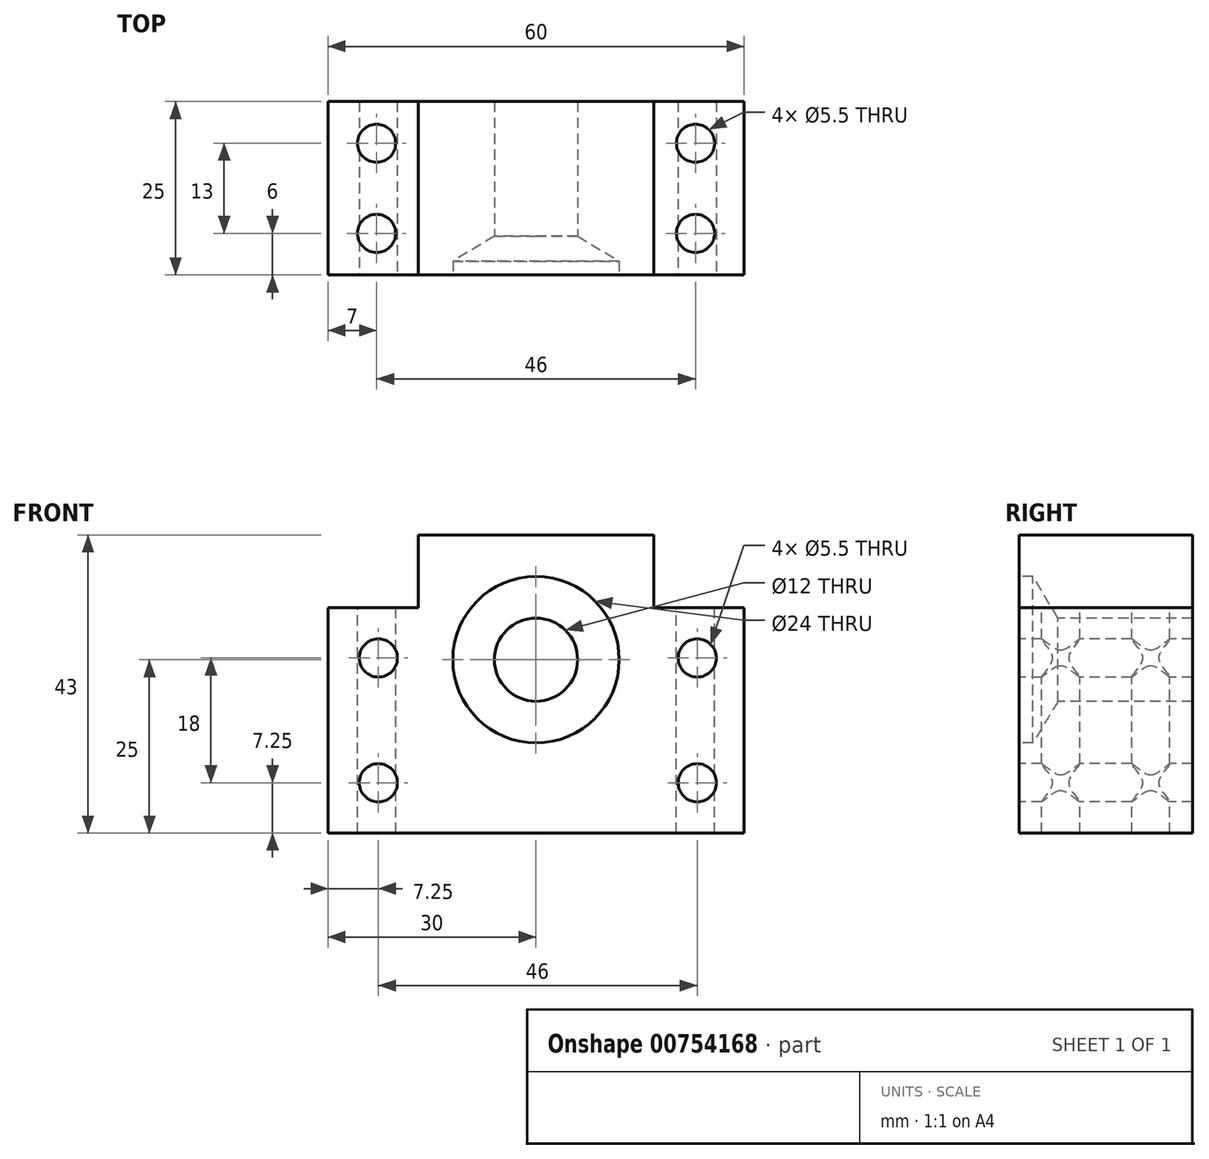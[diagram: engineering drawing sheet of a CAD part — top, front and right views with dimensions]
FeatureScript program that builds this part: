
annotation { "Feature Type Name" : "Feature", "Feature Type Description" : "" }
export const myFeature = defineFeature(function(context is Context, id is Id, definition is map)
    precondition{}
    {
        {
            var Q0;
            Q0=qCreatedBy(makeId("Front.planeOp"),FACE);
            var sketch = newSketch(context, id + "F0", { "sketchPlane" : qUnion([Q0])});
            skLineSegment(sketch, "E0.bottom", {"start": v(0, 0) * mm, "end": v(60, 0) * mm});
            skLineSegment(sketch, "E0.top", {"start": v(0, 43) * mm, "end": v(60, 43) * mm});
            skLineSegment(sketch, "E0.left", {"start": v(0, 0) * mm, "end": v(0, 43) * mm});
            skLineSegment(sketch, "E0.right", {"start": v(60, 0) * mm, "end": v(60, 43) * mm});
            skSolve(sketch);
        }
        {
            var Q0;
            Q0=makeQuery(id+"F0.imprint","IMPRINT",FACE,{"disambiguationData":[TD([[makeQuery(id+"F0.imprint","IMPRINT",EDGE,{"derivedFrom":sQuery(id+"F0.wireOp",EDGE,"E0.bottom")}),1.0]])]});
            var sketch = newSketch(context, id + "F1", { "sketchPlane" : qUnion([Q0])});
            skPoint(sketch, "E1", {"position": v(30, 25) * mm});
            skPoint(sketch, "E2", {"position": v(53.25, 7.25) * mm});
            skPoint(sketch, "E3", {"position": v(7.25, 7.25) * mm});
            skPoint(sketch, "E4", {"position": v(7.25, 25.25) * mm});
            skPoint(sketch, "E5", {"position": v(53.25, 25.25) * mm});
            skSolve(sketch);
        }
        {
            var Q0;
            Q0=makeQuery(id+"F0.imprint","IMPRINT",FACE,{"disambiguationData":[TD([[makeQuery(id+"F0.imprint","IMPRINT",EDGE,{"derivedFrom":sQuery(id+"F0.wireOp",EDGE,"E0.bottom")}),1.0]])]});
            extrude(context, id + "F2", {"entities" : qUnion([Q0]), "depth" : -25 * mm, "offsetDistance" : 25 * mm});
        }
        {
            var Q0;
            Q0=sQuery(id+"F1.wireOp",VERTEX,"E1");
            var Q1;
            Q1=makeQuery(id+"F2.opExtrude","SWEPT_BODY",BODY,{"disambiguationData":[OSD([sQuery(id+"F0.wireOp",EDGE,"E0.bottom"),sQuery(id+"F0.wireOp",EDGE,"E0.top"),sQuery(id+"F0.wireOp",EDGE,"E0.left"),sQuery(id+"F0.wireOp",EDGE,"E0.right")])]});
            hole(context, id + "F3", {"style" : HoleStyle.SIMPLE, "endStyle" : HoleEndStyle.THROUGH, "holeDiameter" : 12 * mm, "majorDiameter" : 5 * mm, "isTappedThrough" : true, "tappedDepth" : 12 * mm, "tapClearance" : 3, "startFromSketch" : true, "locations" : qUnion([Q0]), "scope" : qUnion([Q1])});
        }
        {
            var Q0;
            Q0=sQuery(id+"F1.wireOp",VERTEX,"E1");
            var Q1;
            Q1=makeQuery(id+"F2.opExtrude","SWEPT_BODY",BODY,{"disambiguationData":[OSD([sQuery(id+"F0.wireOp",EDGE,"E0.bottom"),sQuery(id+"F0.wireOp",EDGE,"E0.top"),sQuery(id+"F0.wireOp",EDGE,"E0.left"),sQuery(id+"F0.wireOp",EDGE,"E0.right")])]});
            hole(context, id + "F4", {"style" : HoleStyle.SIMPLE, "endStyle" : HoleEndStyle.BLIND, "holeDiameter" : 24 * mm, "majorDiameter" : 5 * mm, "holeDepth" : 2 * mm, "isTappedThrough" : true, "tappedDepth" : 12 * mm, "tapClearance" : 3, "locations" : qUnion([Q0]), "scope" : qUnion([Q1])});
        }
        {
            var Q0;
            Q0=sQuery(id+"F1.wireOp",VERTEX,"E3");
            var Q1;
            Q1=sQuery(id+"F1.wireOp",VERTEX,"E2");
            var Q2;
            Q2=sQuery(id+"F1.wireOp",VERTEX,"E5");
            var Q3;
            Q3=sQuery(id+"F1.wireOp",VERTEX,"E4");
            var Q4;
            Q4=makeQuery(id+"F2.opExtrude","SWEPT_BODY",BODY,{"disambiguationData":[OSD([sQuery(id+"F0.wireOp",EDGE,"E0.bottom"),sQuery(id+"F0.wireOp",EDGE,"E0.top"),sQuery(id+"F0.wireOp",EDGE,"E0.left"),sQuery(id+"F0.wireOp",EDGE,"E0.right")])]});
            hole(context, id + "F5", {"style" : HoleStyle.SIMPLE, "endStyle" : HoleEndStyle.THROUGH, "holeDiameter" : 5.5 * mm, "majorDiameter" : 5 * mm, "isTappedThrough" : true, "tappedDepth" : 12 * mm, "tapClearance" : 3, "locations" : qUnion([Q0, Q1, Q2, Q3]), "scope" : qUnion([Q4])});
        }
        {
            var Q0;
            Q0=makeQuery(id+"F2.opExtrude","SWEPT_FACE",FACE,{"disambiguationData":[OSD([sQuery(id+"F0.wireOp",EDGE,"E0.top")])]});
            var sketch = newSketch(context, id + "F6", { "sketchPlane" : qUnion([Q0])});
            skPoint(sketch, "E6", {"position": v(7, 19) * mm});
            skPoint(sketch, "E7", {"position": v(7, 6) * mm});
            skPoint(sketch, "E8", {"position": v(53, 6) * mm});
            skPoint(sketch, "E9", {"position": v(53, 19) * mm});
            skLineSegment(sketch, "E10", {"start": v(13, 25) * mm, "end": v(13, 0) * mm});
            skLineSegment(sketch, "E11", {"start": v(47, 25) * mm, "end": v(47, 0) * mm});
            skSolve(sketch);
        }
        {
            var Q0;
            Q0=sQuery(id+"F6.wireOp",VERTEX,"E7");
            var Q1;
            Q1=sQuery(id+"F6.wireOp",VERTEX,"E8");
            var Q2;
            Q2=sQuery(id+"F6.wireOp",VERTEX,"E9");
            var Q3;
            Q3=sQuery(id+"F6.wireOp",VERTEX,"E6");
            var Q4;
            Q4=makeQuery(id+"F2.opExtrude","SWEPT_BODY",BODY,{"disambiguationData":[OSD([sQuery(id+"F0.wireOp",EDGE,"E0.bottom"),sQuery(id+"F0.wireOp",EDGE,"E0.top"),sQuery(id+"F0.wireOp",EDGE,"E0.left"),sQuery(id+"F0.wireOp",EDGE,"E0.right")])]});
            hole(context, id + "F7", {"style" : HoleStyle.SIMPLE, "endStyle" : HoleEndStyle.THROUGH, "holeDiameter" : 5.5 * mm, "majorDiameter" : 5 * mm, "isTappedThrough" : true, "tappedDepth" : 12 * mm, "tapClearance" : 3, "locations" : qUnion([Q0, Q1, Q2, Q3]), "scope" : qUnion([Q4])});
        }
        {
            var Q0;
            {var subQ0=sQuery(id+"F6.wireOp",EDGE,"E10");Q0=makeQuery(id+"F6.imprint","IMPRINT",FACE,{"disambiguationData":[TD([[makeQuery(id+"F6.imprint","IMPRINT",EDGE,{"derivedFrom":subQ0}),-1.0]])]});}
            var Q1;
            {var subQ0=sQuery(id+"F6.wireOp",EDGE,"E11");Q1=makeQuery(id+"F6.imprint","IMPRINT",FACE,{"disambiguationData":[TD([[makeQuery(id+"F6.imprint","IMPRINT",EDGE,{"derivedFrom":subQ0}),1.0]])]});}
            extrude(context, id + "F8", {"entities" : qUnion([Q0, Q1]), "operationType" : NewBodyOperationType.REMOVE, "oppositeDirection" : true, "depth" : 10.5 * mm, "offsetDistance" : 25 * mm});
        }
    });
